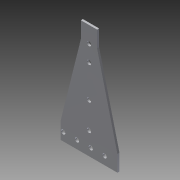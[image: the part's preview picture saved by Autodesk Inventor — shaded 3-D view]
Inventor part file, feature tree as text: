
AUTODESK INVENTOR PART (.ipt)
format: ipt  version: 2013 (Build 170138000, 138)  size: 129,536 bytes
history: native  units: in
note: dims shown in document units (in); Inventor stores cm internally (conversion verified against a paired STEP export)
features: extrude x5, sketch x5, reference x5
ambient origin geometry x8: Origin, YZ Plane, XZ Plane, XY Plane, X Axis, Y Axis, Z Axis, Center Point
bodies: Solid1 (feature_tree)
feature tree (15):
  extrude  "Extrusion1"  Depth=1.0in
  extrude  "Extrusion2"  Depth=1.25in
  extrude  "Extrusion3"  Depth=0.125in
  extrude  "Extrusion4"  Depth=1.0in
  extrude  "Extrusion5"  Depth=0.266in
  sketch  "Sketch1"  dims[d0=7.0in d3=1.0in]
  sketch  "Sketch2"  dims[d4=1.25in d5=1.25in]
  sketch  "Sketch4"  dims[d6=1.0in d7=0.125in]
  reference  "Reference1"
  reference  "Reference2"
  reference  "Reference3"
  reference  "Reference4"
  reference  "Reference5"
  sketch  "Sketch5"  dims[d8=0.125in d9=0.0in d10=1.0in]
  sketch  "Sketch6"  dims[d11=1.0in d12=0.266in d13=0.266in d14=1.0in d15=0.0in d16=1.0in d20=1.0in d21=0.0in d22=2.0in d23=0.266in d24=1.0in d25=0.0in d26=1.625in d27=0.266in d28=1.0in d29=0.0in]
